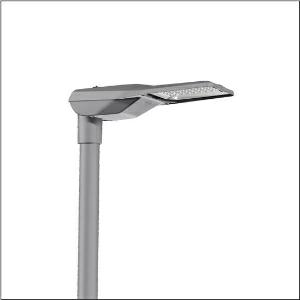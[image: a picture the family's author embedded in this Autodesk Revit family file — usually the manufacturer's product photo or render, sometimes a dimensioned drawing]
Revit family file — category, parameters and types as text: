
# Revit family: streetlight_sl_21_iq_mini___st1_0ab_5xe2m31v08jb_8772
name_source: partatom
category: Lighting Fixtures
units: mm (PartAtom-declared; Revit-internal decimal feet)

## family parameters
Cut with Voids When Loaded = No
Host = Face
Light Source = No
Part Type = Normal
Room Calculation Point = No
Round Connector Dimension = Use Diameter
Shared = No

## types (1)
- --- (1 x LED, 9870 lm, 72.5 W, 3000K)
    Apparent Load = 73 VA
    CIE Flux Codes = 40 74 97 100 100
    Color Rendering = 70
    Color Temperature = 3000K
    Default Elevation = 1800 mm
    Description = Streetlight SL 21 iQ mini, mast luminaire, primary light control with lens, of PMMA, primary optical cover: cover, of toughened safety glass, transparent, light distribution: ST1.0aB, light emission: direct distribution, primary light characteristic: asymmetric, installation type: post-top, side-entry, LED, High Power LED, rated luminous flux: 9.870lm, luminous efficacy: 136lm/W, light colour: 730, colour temperature: 3000K, control: presetting dimming logarithmic, Street-Remote, Auto-Match, Temp-Guard, Lumen-Switch, Night-Set, Smart-Wire, Light-Fading, Desk-Remote (wireless, voltage-free reading and setting of iQ features in the workshop via application-optimized NFC function/RFID function), optimised constant luminous flux control (CLO 2.0), mains connection: 220..240V, AC, 50/60Hz, start of lifetime: 73W, end of service life: 76W, reduction: 33W, luminaire housing, of diecast aluminium, powder-coated, Siteco® metallic grey (DB 702S), corrosivity category C5 mid according to DIN EN ISO 12944, please order mast flange separately, inclination adjustable: 0°, 5°, 10°, 15°, sealing non-destructively replaceable, multi-level sealing system, length: 628mm, width: 235mm, height: 110mm, mast flange for spigot size: 42mm (side-entry): 5XC10008XM4, 60/48mm (side-entry/post-top): 5XC10108XM2, 76/60mm (side-entry/post-top): 5XC10108XM1, Smart Interface above, protection rating (complete): IP66, insulation class (complete): insulation class II (safety insulation), certification: CE, ENEC, ENEC+, VDE, impact resistance: IK09, permissible operating ambient temperature for outdoor applications: -40..+50°C, standard-compliant lighting for roads and squares, packaging unit: 1 piece

Light Distribution: ST1.0aB
    Height = 110 mm
    Lamp = 1 x LED
    Lamp Light Flux = 9870 lm
    Lamp Power = 72.5 W
    Lamp count = 1
    Length = 625 mm
    Luminous efficacy = 136 lm/W
    Manufacturer = Siteco
    ModVariant = No
    Model = 5XE2M31V08JB
    Number of Poles = 1
    OnlyDefault = Yes
    Power Factor = 1
    Product Name = Streetlight SL 21 iQ mini | ST1.0aB
    Product group = mast luminaire | pylon top
    ProductGroupID = 6100
    Protection Class = Protection class II
    Protection Degree = IP 66
    RLX_Detail_Level = 1
    RLX_Emergency_Light_Flux = 0 lm
    RLX_Emergency_Type = 0
    RLX_Emergency_Type_DB = No
    RlxData = <blob elided: 94041 chars, md5=d097cc9c>
    Socket = socket
    Standby Power = 0 W
    System Light Flux = 9870 lm
    System Power = 73 W
    Type Comments = factory setting: luminous flux: 100 % | dim-lin: 254 | 755 mA
    Type Image = l_1003515.jpg
    URL = http://relux.com
    VarID = @adj_042293
    Voltage = 0 V
    Weight = 0.00 kg
    Width = 234 mm

## geometry (parser evidence)
native form markers: Blend x4, Sweep x10
no freeform markers — native parametric forms only
